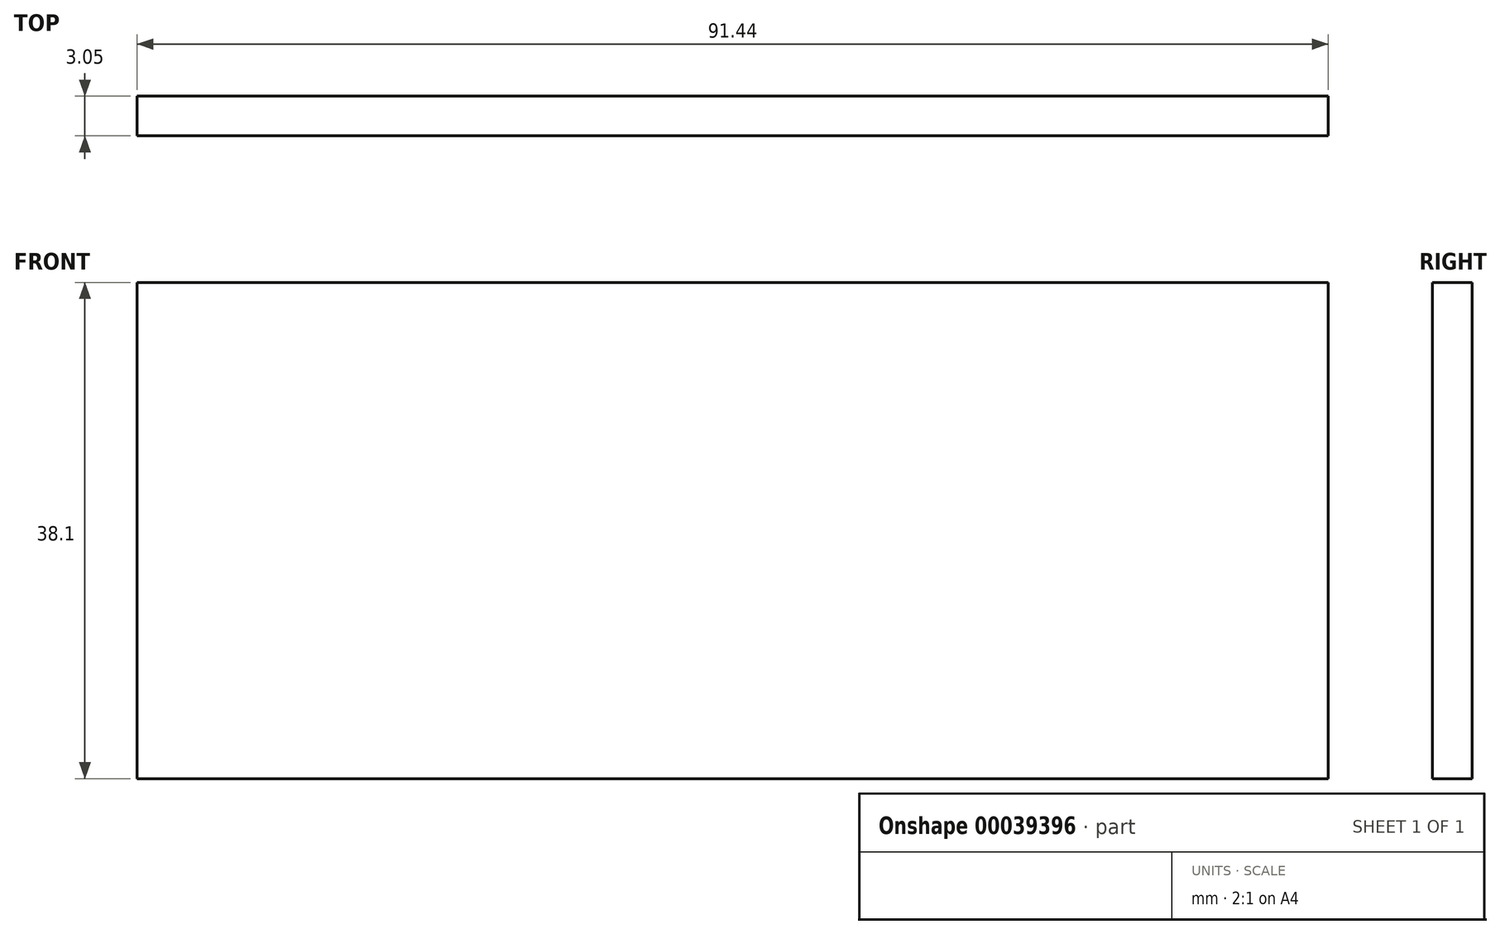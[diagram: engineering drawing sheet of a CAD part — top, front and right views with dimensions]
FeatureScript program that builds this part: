
annotation { "Feature Type Name" : "Feature", "Feature Type Description" : "" }
export const myFeature = defineFeature(function(context is Context, id is Id, definition is map)
    precondition{}
    {
        {
            var Q0;
            Q0=qCreatedBy(makeId("Front.planeOp"),FACE);
            var sketch = newSketch(context, id + "F0", { "sketchPlane" : qUnion([Q0])});
            skLineSegment(sketch, "E0.bottom", {"start": v(0, 0) * mm, "end": v(91.44, 0) * mm});
            skLineSegment(sketch, "E0.top", {"start": v(0, 38.1) * mm, "end": v(91.44, 38.1) * mm});
            skLineSegment(sketch, "E0.left", {"start": v(0, 0) * mm, "end": v(0, 38.1) * mm});
            skLineSegment(sketch, "E0.right", {"start": v(91.44, 0) * mm, "end": v(91.44, 38.1) * mm});
            skSolve(sketch);
        }
        {
            var Q0;
            Q0=makeQuery(id+"F0.imprint","IMPRINT",FACE,{"disambiguationData":[TD([[makeQuery(id+"F0.imprint","IMPRINT",EDGE,{"derivedFrom":sQuery(id+"F0.wireOp",EDGE,"E0.bottom")}),1.0]])]});
            extrude(context, id + "F1", {"entities" : qUnion([Q0]), "depth" : 3.05 * mm});
        }
    });
